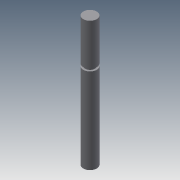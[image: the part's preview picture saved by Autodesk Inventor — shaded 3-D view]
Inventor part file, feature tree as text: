
AUTODESK INVENTOR PART (.ipt)
format: ipt  version: 2013 (Build 170138000, 138)  size: 73,216 bytes
history: native  units: mm
features: sketch x2, revolve x1
ambient origin geometry x8: Origin, YZ Plane, XZ Plane, XY Plane, X Axis, Y Axis, Z Axis, Center Point
bodies: Solid1 (feature_tree)
feature tree (3):
  sketch  "Sketch1"  dims[d6=0.85mm d7=1.0mm]
  revolve  "Revolution1"  [1 undecoded]
  sketch  "Sketch2"  dims[d8=90.0deg]
note: 1 required parameter value undecoded (feature->parameter linkage not recoverable at this tier; creation-order binding heuristic only, values carry confidence <= 0.55)
